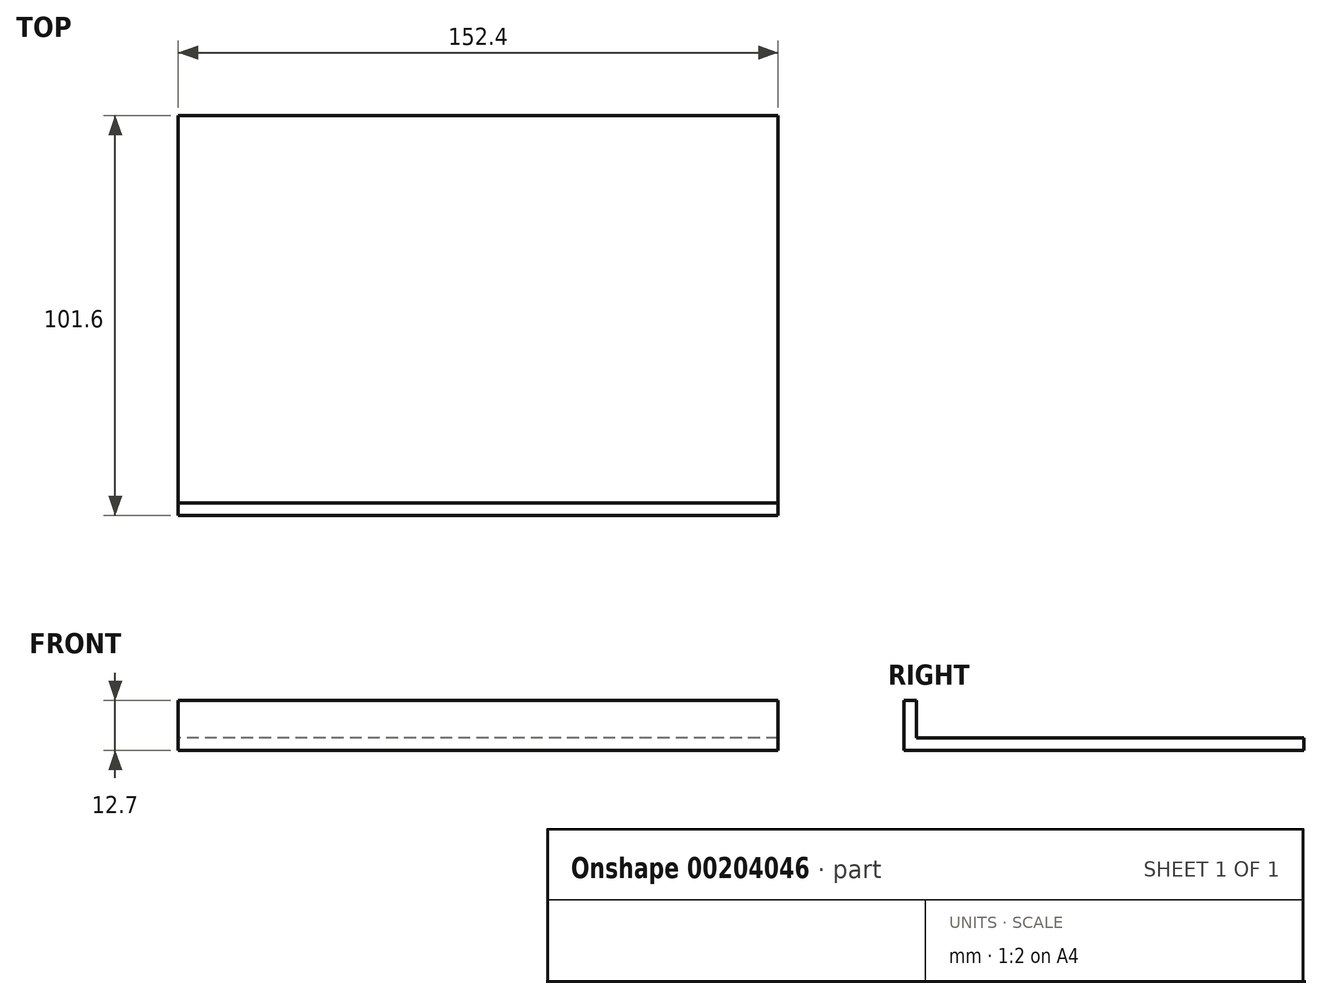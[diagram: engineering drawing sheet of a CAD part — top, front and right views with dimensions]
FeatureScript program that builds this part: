
annotation { "Feature Type Name" : "Feature", "Feature Type Description" : "" }
export const myFeature = defineFeature(function(context is Context, id is Id, definition is map)
    precondition{}
    {
        {
            var Q0;
            Q0=qCreatedBy(makeId("Top.planeOp"),FACE);
            var sketch = newSketch(context, id + "F0", { "sketchPlane" : qUnion([Q0])});
            skLineSegment(sketch, "E0.bottom", {"start": v(76.2, -50.8) * mm, "end": v(-76.2, -50.8) * mm});
            skLineSegment(sketch, "E0.top", {"start": v(76.2, 50.8) * mm, "end": v(-76.2, 50.8) * mm});
            skLineSegment(sketch, "E0.left", {"start": v(76.2, -50.8) * mm, "end": v(76.2, 50.8) * mm});
            skLineSegment(sketch, "E0.right", {"start": v(-76.2, -50.8) * mm, "end": v(-76.2, 50.8) * mm});
            skPoint(sketch, "E0.middle", {"position": v(0, 0) * mm});
            skSolve(sketch);
        }
        {
            var Q0;
            Q0 = qSketchRegion(id + "F0", true);
            extrude(context, id + "F1", {"entities" : qUnion([Q0]), "depth" : 12.7 * mm});
        }
        {
            var Q0;
            Q0=makeQuery(id+"F1.opExtrude","SWEPT_FACE",FACE,{"disambiguationData":[OSD([sQuery(id+"F0.wireOp",EDGE,"E0.right")])]});
            var Q1;
            Q1=makeQuery(id+"F1.opExtrude","CAP_FACE",FACE,{"disambiguationData":[OSD([sQuery(id+"F0.wireOp",EDGE,"E0.bottom"),sQuery(id+"F0.wireOp",EDGE,"E0.top"),sQuery(id+"F0.wireOp",EDGE,"E0.left"),sQuery(id+"F0.wireOp",EDGE,"E0.right")])],"isStart":false});
            var Q2;
            Q2=makeQuery(id+"F1.opExtrude","SWEPT_FACE",FACE,{"disambiguationData":[OSD([sQuery(id+"F0.wireOp",EDGE,"E0.left")])]});
            var Q3;
            Q3=makeQuery(id+"F1.opExtrude","SWEPT_FACE",FACE,{"disambiguationData":[OSD([sQuery(id+"F0.wireOp",EDGE,"E0.top")])]});
            shell(context, id + "F2", {"entities" : qUnion([Q0, Q1, Q2, Q3]), "thickness" : 3.17 * mm});
        }
    });
